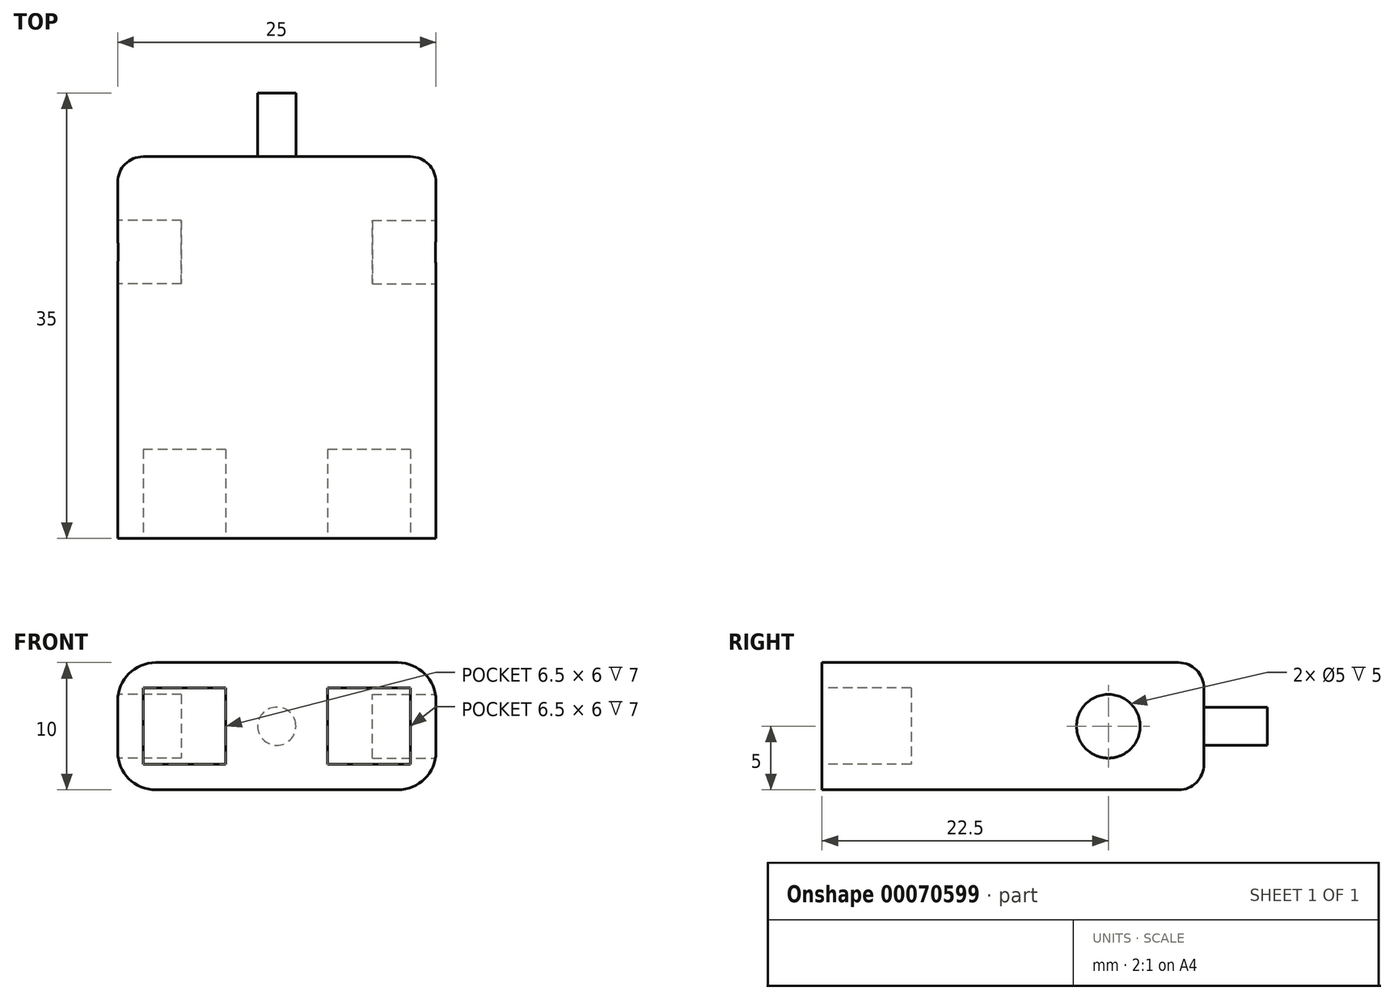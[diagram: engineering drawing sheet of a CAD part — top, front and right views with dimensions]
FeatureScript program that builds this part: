
annotation { "Feature Type Name" : "Feature", "Feature Type Description" : "" }
export const myFeature = defineFeature(function(context is Context, id is Id, definition is map)
    precondition{}
    {
        {
            var Q0;
            Q0=qCreatedBy(makeId("Top.planeOp"),FACE);
            var sketch = newSketch(context, id + "F0", { "sketchPlane" : qUnion([Q0])});
            skLineSegment(sketch, "E0.rect.bottom", {"start": v(-12.5, 15) * mm, "end": v(12.5, 15) * mm});
            skLineSegment(sketch, "E0.rect.top", {"start": v(-12.5, -15) * mm, "end": v(12.5, -15) * mm});
            skLineSegment(sketch, "E0.rect.left", {"start": v(-12.5, 15) * mm, "end": v(-12.5, -15) * mm});
            skLineSegment(sketch, "E0.rect.right", {"start": v(12.5, 15) * mm, "end": v(12.5, -15) * mm});
            skPoint(sketch, "E0.rect.middle", {"position": v(0, 0) * mm});
            skSolve(sketch);
        }
        {
            var Q0;
            Q0=makeQuery(id+"F0.imprint","IMPRINT",FACE,{"disambiguationData":[TD([[makeQuery(id+"F0.imprint","IMPRINT",EDGE,{"derivedFrom":sQuery(id+"F0.wireOp",EDGE,"E0.rect.bottom")}),-1.0]])]});
            extrude(context, id + "F1", {"entities" : qUnion([Q0]), "depth" : 10 * mm});
        }
        {
            var Q0;
            Q0=makeQuery(id+"F1.opExtrude","SWEPT_FACE",FACE,{"disambiguationData":[OSD([sQuery(id+"F0.wireOp",EDGE,"E0.rect.bottom")])]});
            var sketch = newSketch(context, id + "F2", { "sketchPlane" : qUnion([Q0])});
            skCircle(sketch, "E1", {"center": v(0, 5) * mm, "radius": 1.5 * mm});
            skSolve(sketch);
        }
        {
            var Q0;
            Q0=makeQuery(id+"F2.imprint","IMPRINT",FACE,{"disambiguationData":[TD([[makeQuery(id+"F2.imprint","IMPRINT",EDGE,{"derivedFrom":sQuery(id+"F2.wireOp",EDGE,"E1")}),1.0]])]});
            extrude(context, id + "F3", {"entities" : qUnion([Q0]), "operationType" : NewBodyOperationType.ADD, "depth" : 5 * mm});
        }
        {
            var Q0;
            Q0=makeQuery(id+"F1.opExtrude","SWEPT_FACE",FACE,{"disambiguationData":[OSD([sQuery(id+"F0.wireOp",EDGE,"E0.rect.right")])]});
            var sketch = newSketch(context, id + "F4", { "sketchPlane" : qUnion([Q0])});
            skCircle(sketch, "E2", {"center": v(7.5, 5) * mm, "radius": 2.5 * mm});
            skSolve(sketch);
        }
        {
            var Q0;
            Q0=makeQuery(id+"F4.imprint","IMPRINT",FACE,{"disambiguationData":[TD([[makeQuery(id+"F4.imprint","IMPRINT",EDGE,{"derivedFrom":sQuery(id+"F4.wireOp",EDGE,"E2")}),1.0]])]});
            extrude(context, id + "F5", {"entities" : qUnion([Q0]), "operationType" : NewBodyOperationType.REMOVE, "oppositeDirection" : true, "depth" : 5 * mm});
        }
        {
            var Q0;
            Q0=makeQuery(id+"F1.opExtrude","SWEPT_FACE",FACE,{"disambiguationData":[OSD([sQuery(id+"F0.wireOp",EDGE,"E0.rect.left")])]});
            var sketch = newSketch(context, id + "F6", { "sketchPlane" : qUnion([Q0])});
            skCircle(sketch, "E3", {"center": v(-7.5, 5) * mm, "radius": 2.5 * mm});
            skSolve(sketch);
        }
        {
            var Q0;
            Q0=makeQuery(id+"F6.imprint","IMPRINT",FACE,{"disambiguationData":[TD([[makeQuery(id+"F6.imprint","IMPRINT",EDGE,{"derivedFrom":sQuery(id+"F6.wireOp",EDGE,"E3")}),1.0]])]});
            extrude(context, id + "F7", {"entities" : qUnion([Q0]), "operationType" : NewBodyOperationType.REMOVE, "oppositeDirection" : true, "depth" : 5 * mm});
        }
        {
            var Q0;
            Q0=makeQuery(id+"F1.opExtrude","SWEPT_FACE",FACE,{"disambiguationData":[OSD([sQuery(id+"F0.wireOp",EDGE,"E0.rect.top")])]});
            var sketch = newSketch(context, id + "F8", { "sketchPlane" : qUnion([Q0])});
            skLineSegment(sketch, "E4.bottom", {"start": v(10.5, 2) * mm, "end": v(-10.5, 2) * mm});
            skLineSegment(sketch, "E4.top", {"start": v(10.5, 8) * mm, "end": v(-10.5, 8) * mm});
            skLineSegment(sketch, "E4.left", {"start": v(10.5, 2) * mm, "end": v(10.5, 8) * mm});
            skLineSegment(sketch, "E4.right", {"start": v(-10.5, 2) * mm, "end": v(-10.5, 8) * mm});
            skLineSegment(sketch, "E5.bottom", {"start": v(-4, 8) * mm, "end": v(4, 8) * mm});
            skLineSegment(sketch, "E5.top", {"start": v(-4, 2) * mm, "end": v(4, 2) * mm});
            skLineSegment(sketch, "E5.left", {"start": v(-4, 8) * mm, "end": v(-4, 2) * mm});
            skLineSegment(sketch, "E5.right", {"start": v(4, 8) * mm, "end": v(4, 2) * mm});
            skSolve(sketch);
        }
        {
            var Q0;
            {var subQ0=sQuery(id+"F8.wireOp",EDGE,"E4.left");Q0=makeQuery(id+"F8.imprint","IMPRINT",FACE,{"disambiguationData":[TD([[makeQuery(id+"F8.imprint","IMPRINT",EDGE,{"derivedFrom":subQ0}),1.0]])]});}
            var Q1;
            {var subQ0=sQuery(id+"F8.wireOp",EDGE,"E4.right");Q1=makeQuery(id+"F8.imprint","IMPRINT",FACE,{"disambiguationData":[TD([[makeQuery(id+"F8.imprint","IMPRINT",EDGE,{"derivedFrom":subQ0}),-1.0]])]});}
            extrude(context, id + "F9", {"entities" : qUnion([Q0, Q1]), "operationType" : NewBodyOperationType.REMOVE, "oppositeDirection" : true, "depth" : 7 * mm});
        }
        {
            var Q0;
            Q0=makeQuery(id+"F1.opExtrude","CAP_EDGE",EDGE,{"disambiguationData":[OSD([sQuery(id+"F0.wireOp",EDGE,"E0.rect.left")])],"isStart":false});
            var Q1;
            Q1=makeQuery(id+"F1.opExtrude","CAP_EDGE",EDGE,{"disambiguationData":[OSD([sQuery(id+"F0.wireOp",EDGE,"E0.rect.right")])],"isStart":false});
            var Q2;
            Q2=makeQuery(id+"F1.opExtrude","CAP_EDGE",EDGE,{"disambiguationData":[OSD([sQuery(id+"F0.wireOp",EDGE,"E0.rect.right")])],"isStart":true});
            var Q3;
            Q3=makeQuery(id+"F1.opExtrude","CAP_EDGE",EDGE,{"disambiguationData":[OSD([sQuery(id+"F0.wireOp",EDGE,"E0.rect.left")])],"isStart":true});
            fillet(context, id + "F10", {"entities" : qUnion([Q0, Q1, Q2, Q3]), "radius" : 3 * mm, "tangentPropagation" : true, "allowEdgeOverflow" : false});
        }
        {
            var Q0;
            Q0=makeQuery(id+"F10.opFillet","BLEND_EDGE",EDGE,{"blendedFrom":[makeQuery(id+"F1.opExtrude","CAP_EDGE",EDGE,{"disambiguationData":[OSD([sQuery(id+"F0.wireOp",EDGE,"E0.rect.right")])],"isStart":true}),makeQuery(id+"F1.opExtrude","SWEPT_FACE",FACE,{"disambiguationData":[OSD([sQuery(id+"F0.wireOp",EDGE,"E0.rect.bottom")])]})],"blendedInto":[makeQuery(id+"F1.opExtrude","SWEPT_FACE",FACE,{"disambiguationData":[OSD([sQuery(id+"F0.wireOp",EDGE,"E0.rect.bottom")])]})]});
            var Q1;
            Q1=makeQuery(id+"F1.opExtrude","SWEPT_EDGE",EDGE,{"disambiguationData":[OSD([sQuery(id+"F0.wireOp",EDGE,"E0.rect.bottom"),sQuery(id+"F0.wireOp",EDGE,"E0.rect.right")])]});
            var Q2;
            Q2=makeQuery(id+"F10.opFillet","BLEND_EDGE",EDGE,{"blendedFrom":[makeQuery(id+"F1.opExtrude","CAP_EDGE",EDGE,{"disambiguationData":[OSD([sQuery(id+"F0.wireOp",EDGE,"E0.rect.right")])],"isStart":false}),makeQuery(id+"F1.opExtrude","SWEPT_FACE",FACE,{"disambiguationData":[OSD([sQuery(id+"F0.wireOp",EDGE,"E0.rect.bottom")])]})],"blendedInto":[makeQuery(id+"F1.opExtrude","SWEPT_FACE",FACE,{"disambiguationData":[OSD([sQuery(id+"F0.wireOp",EDGE,"E0.rect.bottom")])]})]});
            fillet(context, id + "F11", {"entities" : qUnion([Q0, Q1, Q2]), "radius" : 2 * mm, "tangentPropagation" : true, "allowEdgeOverflow" : false});
        }
    });
